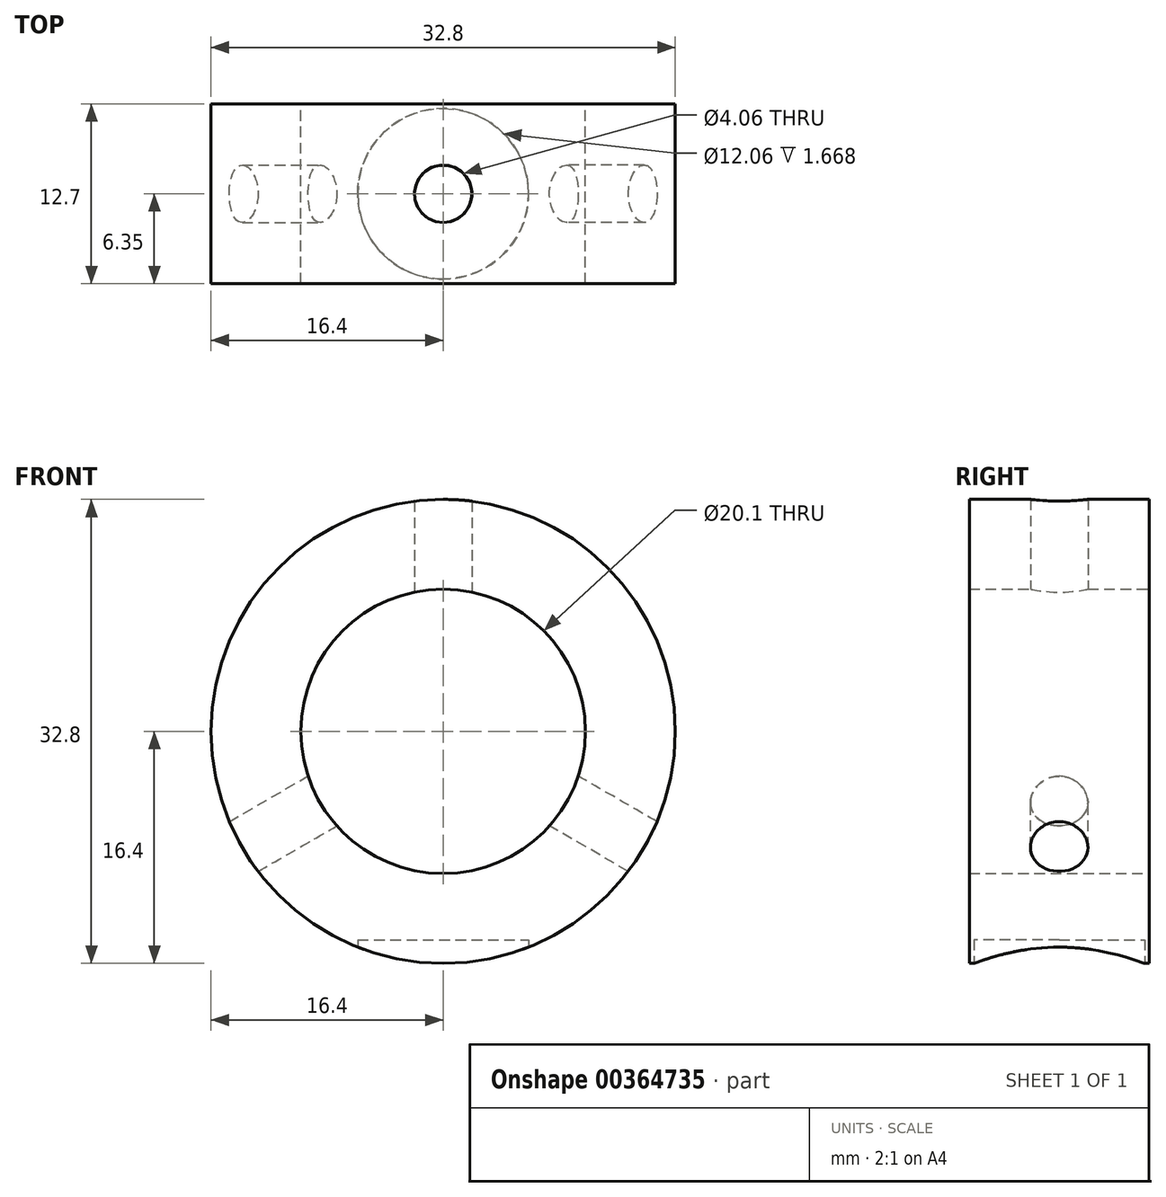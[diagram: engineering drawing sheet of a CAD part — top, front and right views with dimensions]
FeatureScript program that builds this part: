
annotation { "Feature Type Name" : "Feature", "Feature Type Description" : "" }
export const myFeature = defineFeature(function(context is Context, id is Id, definition is map)
    precondition{}
    {
        {
            var Q0;
            Q0=qCreatedBy(makeId("Front.planeOp"),FACE);
            var sketch = newSketch(context, id + "F0", { "sketchPlane" : qUnion([Q0])});
            skCircle(sketch, "E0", {"center": v(0, 0) * mm, "radius": 10.05 * mm});
            skCircle(sketch, "E1", {"center": v(0, 0) * mm, "radius": 16.4 * mm});
            skSolve(sketch);
        }
        {
            var Q0;
            Q0=qSketchRegion(id+"F0",true);
            extrude(context, id + "F1", {"entities" : qUnion([Q0]), "depth" : 12.7 * mm});
        }
        {
            var Q0;
            Q0=qCreatedBy(makeId("Top.planeOp"),FACE);
            var sketch = newSketch(context, id + "F2", { "sketchPlane" : qUnion([Q0])});
            skCircle(sketch, "E2", {"center": v(0, -6.35) * mm, "radius": 2.03 * mm});
            skSolve(sketch);
        }
        {
            var Q0;
            Q0=makeQuery(id+"F2.imprint","IMPRINT",FACE,{"disambiguationData":[TD([[makeQuery(id+"F2.imprint","IMPRINT",EDGE,{"derivedFrom":sQuery(id+"F2.wireOp",EDGE,"E2")}),1.0]])]});
            extrude(context, id + "F3", {"entities" : qUnion([Q0]), "depth" : 25.4 * mm, "offsetDistance" : 25.4 * mm});
        }
        {
            var Q0;
            Q0=makeQuery(id+"F3.opExtrude","SWEPT_BODY",BODY,{"disambiguationData":[OSD([sQuery(id+"F2.wireOp",EDGE,"E2")])]});
            var Q1;
            Q1=makeQuery(id+"F1.opExtrude","SWEPT_FACE",FACE,{"disambiguationData":[OSD([sQuery(id+"F0.wireOp",EDGE,"E0")])]});
            var Q2;
            Q2=makeQuery(id+"F3.opExtrude","SWEPT_BODY",BODY,{"disambiguationData":[OSD([sQuery(id+"F2.wireOp",EDGE,"E2")])]});
            circularPattern(context, id + "F4", {"operationType" : NewBodyOperationType.REMOVE, "entities" : qUnion([Q0]), "axis" : qUnion([Q1]), "angle" : 360 * degree, "instanceCount" : 3, "equalSpace" : true});
        }
        {
            var Q0;
            Q0=qCreatedBy(makeId("Top.planeOp"),FACE);
            cPlane(context, id + "F5", {"entities" : qUnion([Q0]), "cplaneType" : CPlaneType.OFFSET, "offset" : 17.78 * mm, "oppositeDirection" : true, "width" : 152.4 * mm, "height" : 152.4 * mm});
        }
        {
            var Q0;
            Q0=qCreatedBy(id+"F5.planeOp",FACE);
            var sketch = newSketch(context, id + "F6", { "sketchPlane" : qUnion([Q0])});
            skCircle(sketch, "E3", {"center": v(0, -6.35) * mm, "radius": 6.03 * mm});
            skSolve(sketch);
        }
        {
            var Q0;
            Q0=qSketchRegion(id+"F6",true);
            extrude(context, id + "F7", {"entities" : qUnion([Q0]), "operationType" : NewBodyOperationType.REMOVE, "depth" : 3.05 * mm, "offsetDistance" : 25.4 * mm});
        }
    });
